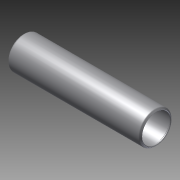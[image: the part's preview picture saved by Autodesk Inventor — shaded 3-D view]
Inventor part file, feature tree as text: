
AUTODESK INVENTOR PART (.ipt)
format: ipt  version: 2012 (Build 160160000, 160)  size: 133,120 bytes
history: native  units: in
note: dims shown in document units (in); Inventor stores cm internally (conversion verified against a paired STEP export)
features: other x42, revolve x1, sketch x1
ambient origin geometry x8: Origin, YZ Plane, XZ Plane, XY Plane, X Axis, Y Axis, Z Axis, Center Point
bodies: Solid1 (feature_tree)
feature tree (44):
  revolve  "Revolution1"  [1 undecoded]
  other  "tube_front_XY"
  other  "tube_front_YZ"
  other  "tube_front_ZX"
  other  "tube_front_X"
  other  "tube_front_Y"
  other  "tube_front_Z"
  other  "tube_front_Center"
  other  "tube_rear_XY"
  other  "tube_rear_YZ"
  other  "tube_rear_ZX"
  other  "tube_rear_X"
  other  "tube_rear_Y"
  other  "tube_rear_Z"
  other  "tube_rear_Center"
  other  "cp1_XY"
  other  "cp1_YZ"
  other  "cp1_ZX"
  other  "cp1_X"
  other  "cp1_Y"
  other  "cp1_Z"
  other  "cp1_Center"
  other  "cp2_XY"
  other  "cp2_YZ"
  other  "cp2_ZX"
  other  "cp2_X"
  other  "cp2_Y"
  other  "cp2_Z"
  other  "cp2_Center"
  other  "cp3_XY"
  other  "cp3_YZ"
  other  "cp3_ZX"
  other  "cp3_X"
  other  "cp3_Y"
  other  "cp3_Z"
  other  "cp3_Center"
  other  "cp4_XY"
  other  "cp4_YZ"
  other  "cp4_ZX"
  other  "cp4_X"
  other  "cp4_Y"
  other  "cp4_Z"
  other  "cp4_Center"
  sketch  "Sketch_1"  dims[d0=360.0deg]
note: 1 required parameter value undecoded (feature->parameter linkage not recoverable at this tier; creation-order binding heuristic only, values carry confidence <= 0.55)
